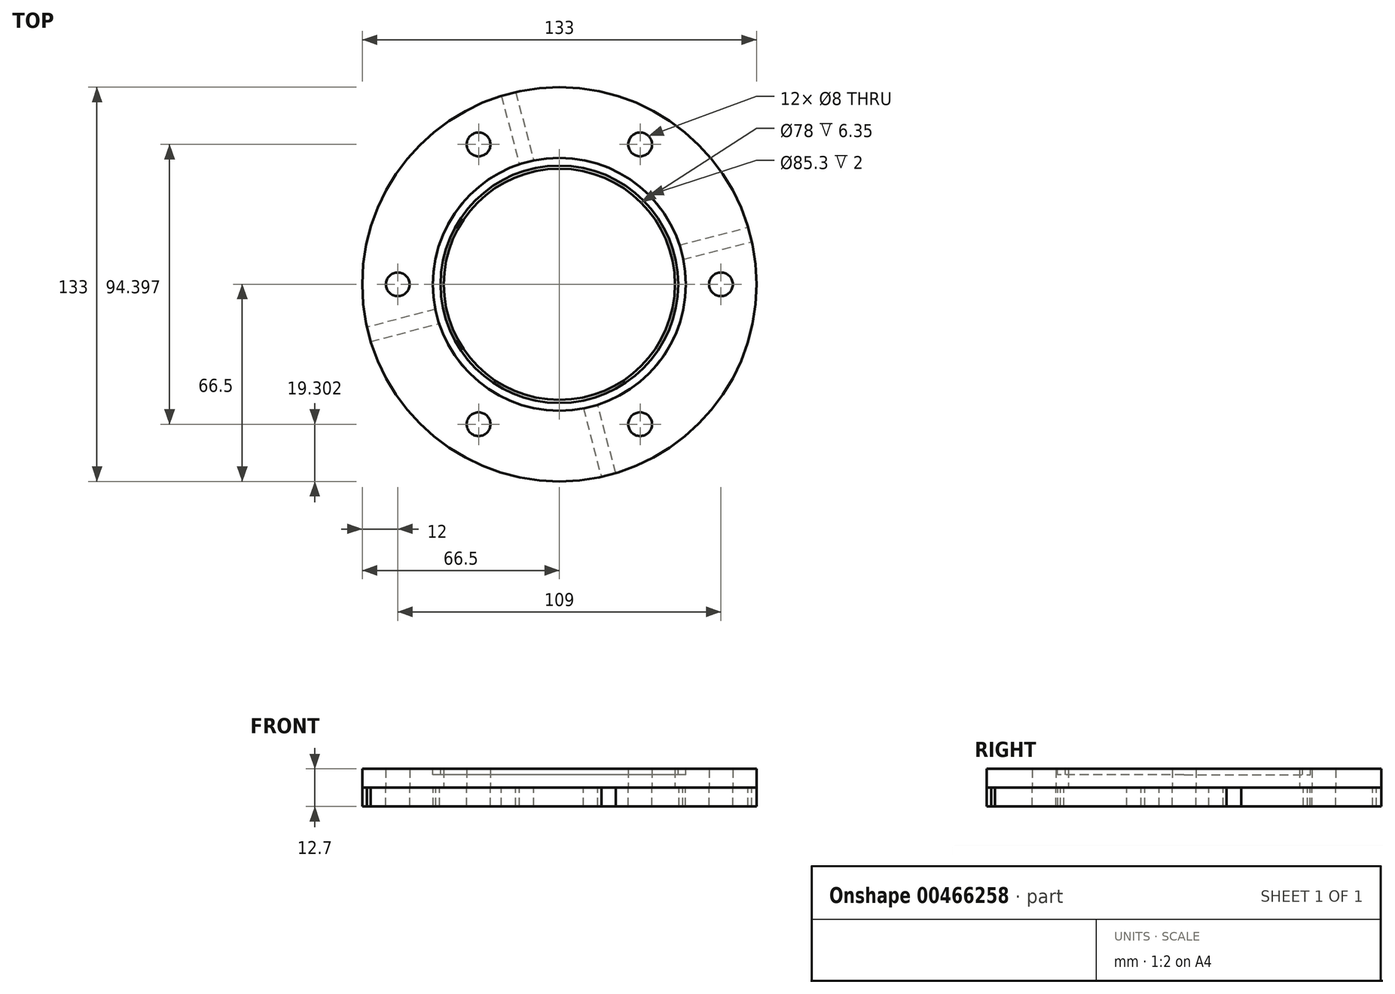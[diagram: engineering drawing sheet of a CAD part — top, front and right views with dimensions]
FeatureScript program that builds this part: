
annotation { "Feature Type Name" : "Feature", "Feature Type Description" : "" }
export const myFeature = defineFeature(function(context is Context, id is Id, definition is map)
    precondition{}
    {
        {
            var Q0;
            Q0=qCreatedBy(makeId("Top.planeOp"),FACE);
            var sketch = newSketch(context, id + "F0", { "sketchPlane" : qUnion([Q0])});
            skCircle(sketch, "E0", {"center": v(0, 0) * mm, "radius": 66.5 * mm});
            skCircle(sketch, "E1", {"center": v(0, 0) * mm, "radius": 39 * mm});
            skCircle(sketch, "E2.cCircle", {"center": v(0, 0) * mm, "radius": 54.5 * mm, "construction": true});
            skLineSegment(sketch, "E2.0", {"start": v(27.25, -47.2) * mm, "end": v(-27.25, -47.2) * mm, "construction": true});
            skLineSegment(sketch, "E2.1", {"start": v(-27.25, -47.2) * mm, "end": v(-54.5, 0) * mm, "construction": true});
            skLineSegment(sketch, "E2.2", {"start": v(-54.5, 0) * mm, "end": v(-27.25, 47.2) * mm, "construction": true});
            skLineSegment(sketch, "E2.3", {"start": v(-27.25, 47.2) * mm, "end": v(27.25, 47.2) * mm, "construction": true});
            skLineSegment(sketch, "E2.4", {"start": v(27.25, 47.2) * mm, "end": v(54.5, 0) * mm, "construction": true});
            skLineSegment(sketch, "E2.5", {"start": v(54.5, 0) * mm, "end": v(27.25, -47.2) * mm, "construction": true});
            skCircle(sketch, "E3", {"center": v(-27.25, 47.2) * mm, "radius": 4 * mm});
            skCircle(sketch, "E4", {"center": v(-54.5, 0) * mm, "radius": 4 * mm});
            skCircle(sketch, "E5", {"center": v(-27.25, -47.2) * mm, "radius": 4 * mm});
            skCircle(sketch, "E6", {"center": v(27.25, -47.2) * mm, "radius": 4 * mm});
            skCircle(sketch, "E7", {"center": v(54.5, 0) * mm, "radius": 4 * mm});
            skCircle(sketch, "E8", {"center": v(27.25, 47.2) * mm, "radius": 4 * mm});
            skSolve(sketch);
        }
        {
            var Q0;
            Q0 = qSketchRegion(id + "F0", true);
            extrude(context, id + "F1", {"entities" : qUnion([Q0]), "depth" : 6.35 * mm});
        }
        {
            var Q0;
            Q0=makeQuery(id+"F1.opExtrude","CAP_FACE",FACE,{"disambiguationData":[OSD([sQuery(id+"F0.wireOp",EDGE,"E0"),sQuery(id+"F0.wireOp",EDGE,"E1"),sQuery(id+"F0.wireOp",EDGE,"E3"),sQuery(id+"F0.wireOp",EDGE,"E4"),sQuery(id+"F0.wireOp",EDGE,"E5"),sQuery(id+"F0.wireOp",EDGE,"E6"),sQuery(id+"F0.wireOp",EDGE,"E7"),sQuery(id+"F0.wireOp",EDGE,"E8")])],"isStart":false});
            var sketch = newSketch(context, id + "F2", { "sketchPlane" : qUnion([Q0])});
            skCircle(sketch, "E9", {"center": v(0, 0) * mm, "radius": 41.35 * mm});
            skSolve(sketch);
        }
        {
            var Q0;
            Q0=qCreatedBy(makeId("Front.planeOp"),FACE);
            var sketch = newSketch(context, id + "F3", { "sketchPlane" : qUnion([Q0])});
            skLineSegment(sketch, "E10.0", {"start": v(-41.35, 6.35) * mm, "end": v(41.35, 6.35) * mm, "construction": true});
            skLineSegment(sketch, "E11.bottom", {"start": v(-40.05, 4.35) * mm, "end": v(-42.65, 4.35) * mm});
            skLineSegment(sketch, "E11.top", {"start": v(-40.05, 8.35) * mm, "end": v(-42.65, 8.35) * mm});
            skLineSegment(sketch, "E11.left", {"start": v(-40.05, 4.35) * mm, "end": v(-40.05, 8.35) * mm});
            skLineSegment(sketch, "E11.right", {"start": v(-42.65, 4.35) * mm, "end": v(-42.65, 8.35) * mm});
            skPoint(sketch, "E11.middle", {"position": v(-41.35, 6.35) * mm});
            skSolve(sketch);
        }
        {
            var Q0;
            Q0 = qSketchRegion(id + "F3", true);
            var Q1;
            Q1=sQuery(id+"F2.wireOp",EDGE,"E9");
            sweep(context, id + "F4", {"profiles" : qUnion([Q0]), "path" : qUnion([Q1])});
        }
        {
            var Q0;
            Q0=makeQuery(id+"F4.opSweep","SWEPT_BODY",BODY,{"disambiguationData":[OSD([sQuery(id+"F2.wireOp",EDGE,"E9"),sQuery(id+"F3.wireOp",EDGE,"E11.bottom"),sQuery(id+"F3.wireOp",EDGE,"E11.top"),sQuery(id+"F3.wireOp",EDGE,"E11.left"),sQuery(id+"F3.wireOp",EDGE,"E11.right")])]});
            var Q1;
            Q1=makeQuery(id+"F1.opExtrude","SWEPT_BODY",BODY,{"disambiguationData":[OSD([sQuery(id+"F0.wireOp",EDGE,"E0"),sQuery(id+"F0.wireOp",EDGE,"E1"),sQuery(id+"F0.wireOp",EDGE,"E3"),sQuery(id+"F0.wireOp",EDGE,"E4"),sQuery(id+"F0.wireOp",EDGE,"E5"),sQuery(id+"F0.wireOp",EDGE,"E6"),sQuery(id+"F0.wireOp",EDGE,"E7"),sQuery(id+"F0.wireOp",EDGE,"E8")])]});
            booleanBodies(context, id + "F5", {"operationType" : BooleanOperationType.SUBTRACTION, "tools" : qUnion([Q0]), "targets" : qUnion([Q1])});
        }
        {
            var Q0;
            Q0=makeQuery(id+"F1.opExtrude","CAP_FACE",FACE,{"disambiguationData":[OSD([sQuery(id+"F0.wireOp",EDGE,"E0"),sQuery(id+"F0.wireOp",EDGE,"E1"),sQuery(id+"F0.wireOp",EDGE,"E3"),sQuery(id+"F0.wireOp",EDGE,"E4"),sQuery(id+"F0.wireOp",EDGE,"E5"),sQuery(id+"F0.wireOp",EDGE,"E6"),sQuery(id+"F0.wireOp",EDGE,"E7"),sQuery(id+"F0.wireOp",EDGE,"E8")])],"isStart":true});
            var sketch = newSketch(context, id + "F6", { "sketchPlane" : qUnion([Q0])});
            skCircle(sketch, "E12", {"center": v(0, 0) * mm, "radius": 42.5 * mm});
            skCircle(sketch, "E13", {"center": v(0, 0) * mm, "radius": 66.5 * mm});
            skCircle(sketch, "E14", {"center": v(54.5, 0) * mm, "radius": 4 * mm});
            skCircle(sketch, "E15", {"center": v(27.25, -47.2) * mm, "radius": 4 * mm});
            skCircle(sketch, "E16", {"center": v(-27.25, -47.2) * mm, "radius": 4 * mm});
            skCircle(sketch, "E17", {"center": v(-54.5, 0) * mm, "radius": 4 * mm});
            skCircle(sketch, "E18", {"center": v(-27.25, 47.2) * mm, "radius": 4 * mm});
            skCircle(sketch, "E19", {"center": v(27.25, 47.2) * mm, "radius": 4 * mm});
            skSolve(sketch);
        }
        {
            var Q0;
            Q0 = qSketchRegion(id + "F6", true);
            extrude(context, id + "F7", {"entities" : qUnion([Q0]), "depth" : 6.35 * mm, "offsetDistance" : 25 * mm});
        }
        {
            var Q0;
            Q0=makeQuery(id+"F7.opExtrude","CAP_FACE",FACE,{"disambiguationData":[OSD([sQuery(id+"F6.wireOp",EDGE,"E12"),sQuery(id+"F6.wireOp",EDGE,"E13"),sQuery(id+"F6.wireOp",EDGE,"E14"),sQuery(id+"F6.wireOp",EDGE,"E15"),sQuery(id+"F6.wireOp",EDGE,"E16"),sQuery(id+"F6.wireOp",EDGE,"E17"),sQuery(id+"F6.wireOp",EDGE,"E18"),sQuery(id+"F6.wireOp",EDGE,"E19")])],"isStart":false});
            var sketch = newSketch(context, id + "F8", { "sketchPlane" : qUnion([Q0])});
            skLineSegment(sketch, "E20", {"start": v(64.92, -14.4) * mm, "end": v(41.68, -8.32) * mm});
            skLineSegment(sketch, "E21", {"start": v(63.65, -19.25) * mm, "end": v(40.41, -13.16) * mm});
            skLineSegment(sketch, "E22", {"start": v(0, 0) * mm, "end": v(64.33, -16.84) * mm, "construction": true});
            skLineSegment(sketch, "E23", {"start": v(64.92, -14.4) * mm, "end": v(66.85, -14.92) * mm});
            skLineSegment(sketch, "E24", {"start": v(65.59, -19.75) * mm, "end": v(66.85, -14.92) * mm});
            skLineSegment(sketch, "E25", {"start": v(65.59, -19.75) * mm, "end": v(63.65, -19.25) * mm});
            skLineSegment(sketch, "E26", {"start": v(64.33, -16.84) * mm, "end": v(66.22, -17.33) * mm, "construction": true});
            skLineSegment(sketch, "E27", {"start": v(40.41, -13.16) * mm, "end": v(38.48, -12.66) * mm});
            skLineSegment(sketch, "E28", {"start": v(38.48, -12.66) * mm, "end": v(39.74, -7.82) * mm});
            skLineSegment(sketch, "E29", {"start": v(39.74, -7.82) * mm, "end": v(41.68, -8.32) * mm});
            skCircle(sketch, "E30.0", {"center": v(27.25, -47.2) * mm, "radius": 4 * mm, "construction": true});
            skCircle(sketch, "E31.0", {"center": v(54.5, 0) * mm, "radius": 4 * mm, "construction": true});
            skPoint(sketch, "E32.center", {"position": v(-0.08, -0.23) * mm});
            skLineSegment(sketch, "E33.1.0", {"start": v(12.5, 38.85) * mm, "end": v(7.65, 40.11) * mm});
            skLineSegment(sketch, "E33.1.1", {"start": v(14.24, 65.29) * mm, "end": v(8.16, 42.05) * mm});
            skLineSegment(sketch, "E33.1.2", {"start": v(19.08, 64.02) * mm, "end": v(13, 40.78) * mm});
            skLineSegment(sketch, "E33.1.3", {"start": v(19.59, 65.96) * mm, "end": v(14.75, 67.22) * mm});
            skLineSegment(sketch, "E33.1.4", {"start": v(14.24, 65.29) * mm, "end": v(14.75, 67.22) * mm});
            skLineSegment(sketch, "E33.1.5", {"start": v(7.65, 40.11) * mm, "end": v(8.16, 42.05) * mm});
            skLineSegment(sketch, "E33.1.6", {"start": v(19.59, 65.96) * mm, "end": v(19.08, 64.02) * mm});
            skLineSegment(sketch, "E33.1.7", {"start": v(13, 40.78) * mm, "end": v(12.5, 38.85) * mm});
            skLineSegment(sketch, "E33.1.8", {"start": v(-0.16, 0.37) * mm, "end": v(16.67, 64.7) * mm, "construction": true});
            skLineSegment(sketch, "E33.1.9", {"start": v(16.67, 64.7) * mm, "end": v(17.17, 66.6) * mm, "construction": true});
            skLineSegment(sketch, "E33.2.0", {"start": v(-39.01, 12.86) * mm, "end": v(-40.28, 8.02) * mm});
            skLineSegment(sketch, "E33.2.1", {"start": v(-65.45, 14.61) * mm, "end": v(-42.21, 8.53) * mm});
            skLineSegment(sketch, "E33.2.2", {"start": v(-64.19, 19.45) * mm, "end": v(-40.94, 13.37) * mm});
            skLineSegment(sketch, "E33.2.3", {"start": v(-66.12, 19.96) * mm, "end": v(-67.39, 15.12) * mm});
            skLineSegment(sketch, "E33.2.4", {"start": v(-65.45, 14.61) * mm, "end": v(-67.39, 15.12) * mm});
            skLineSegment(sketch, "E33.2.5", {"start": v(-40.28, 8.02) * mm, "end": v(-42.21, 8.53) * mm});
            skLineSegment(sketch, "E33.2.6", {"start": v(-66.12, 19.96) * mm, "end": v(-64.19, 19.45) * mm});
            skLineSegment(sketch, "E33.2.7", {"start": v(-40.94, 13.37) * mm, "end": v(-39.01, 12.86) * mm});
            skLineSegment(sketch, "E33.2.8", {"start": v(-0.53, 0.2) * mm, "end": v(-64.87, 17.04) * mm, "construction": true});
            skLineSegment(sketch, "E33.2.9", {"start": v(-64.87, 17.04) * mm, "end": v(-66.76, 17.54) * mm, "construction": true});
            skLineSegment(sketch, "E33.3.0", {"start": v(-13.03, -38.64) * mm, "end": v(-8.19, -39.9) * mm});
            skLineSegment(sketch, "E33.3.1", {"start": v(-14.78, -65.08) * mm, "end": v(-8.7, -41.84) * mm});
            skLineSegment(sketch, "E33.3.2", {"start": v(-19.62, -63.82) * mm, "end": v(-13.53, -40.58) * mm});
            skLineSegment(sketch, "E33.3.3", {"start": v(-20.12, -65.75) * mm, "end": v(-15.29, -67.02) * mm});
            skLineSegment(sketch, "E33.3.4", {"start": v(-14.78, -65.08) * mm, "end": v(-15.29, -67.02) * mm});
            skLineSegment(sketch, "E33.3.5", {"start": v(-8.19, -39.9) * mm, "end": v(-8.7, -41.84) * mm});
            skLineSegment(sketch, "E33.3.6", {"start": v(-20.12, -65.75) * mm, "end": v(-19.62, -63.82) * mm});
            skLineSegment(sketch, "E33.3.7", {"start": v(-13.53, -40.58) * mm, "end": v(-13.03, -38.64) * mm});
            skLineSegment(sketch, "E33.3.8", {"start": v(-0.37, -0.16) * mm, "end": v(-17.2, -64.5) * mm, "construction": true});
            skLineSegment(sketch, "E33.3.9", {"start": v(-17.2, -64.5) * mm, "end": v(-17.7, -66.39) * mm, "construction": true});
            skPoint(sketch, "E33.center", {"position": v(-0.27, 0.1) * mm});
            skCircle(sketch, "E34.0", {"center": v(-27.25, -47.2) * mm, "radius": 4 * mm, "construction": true});
            skCircle(sketch, "E35.0", {"center": v(-54.5, 0) * mm, "radius": 4 * mm, "construction": true});
            skCircle(sketch, "E36.0", {"center": v(-27.25, 47.2) * mm, "radius": 4 * mm, "construction": true});
            skCircle(sketch, "E37.0", {"center": v(27.25, 47.2) * mm, "radius": 4 * mm, "construction": true});
            skSolve(sketch);
        }
        {
            var Q0;
            Q0 = qSketchRegion(id + "F8", true);
            extrude(context, id + "F9", {"entities" : qUnion([Q0]), "operationType" : NewBodyOperationType.REMOVE, "endBound" : BoundingType.UP_TO_NEXT, "oppositeDirection" : true, "depth" : 25 * mm, "offsetDistance" : 25 * mm});
        }
    });
